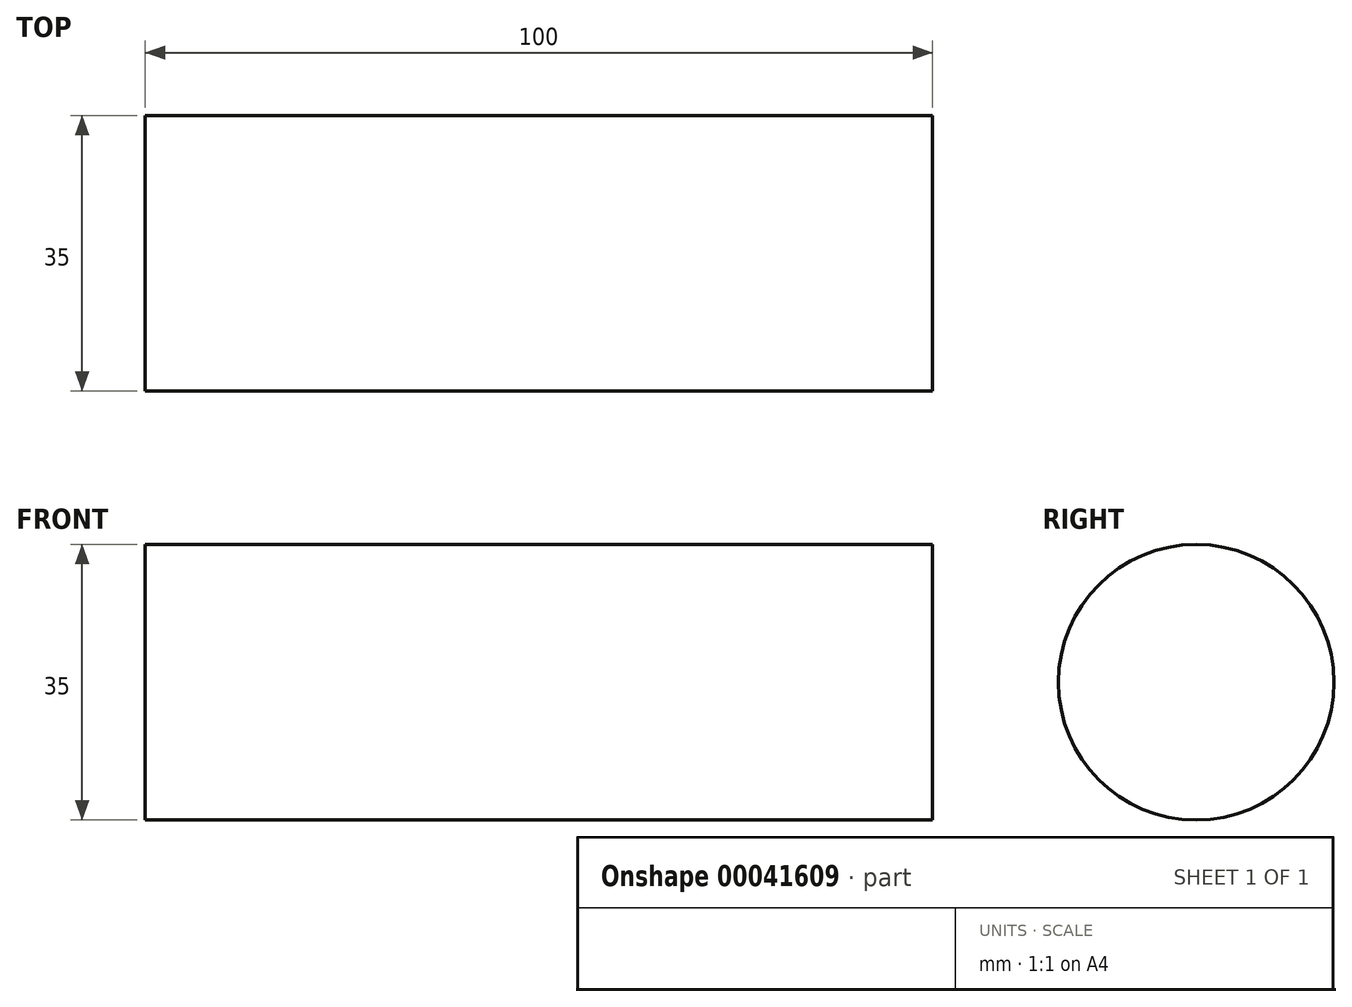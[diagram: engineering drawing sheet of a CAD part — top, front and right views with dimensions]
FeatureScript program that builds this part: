
annotation { "Feature Type Name" : "Feature", "Feature Type Description" : "" }
export const myFeature = defineFeature(function(context is Context, id is Id, definition is map)
    precondition{}
    {
        {
            var Q0;
            Q0=qCreatedBy(makeId("Front.planeOp"),FACE);
            var sketch = newSketch(context, id + "F0", { "sketchPlane" : qUnion([Q0])});
            skLineSegment(sketch, "E0.rect.bottom", {"start": v(100, 17.5) * mm, "end": v(0, 17.5) * mm});
            skLineSegment(sketch, "E0.rect.top", {"start": v(100, -17.5) * mm, "end": v(0, -17.5) * mm, "construction": true});
            skLineSegment(sketch, "E0.rect.left", {"start": v(100, 17.5) * mm, "end": v(100, -17.5) * mm, "construction": true});
            skLineSegment(sketch, "E0.rect.right", {"start": v(0, 17.5) * mm, "end": v(0, -17.5) * mm, "construction": true});
            skPoint(sketch, "E0.rect.middle", {"position": v(50, 0) * mm});
            skLineSegment(sketch, "E1", {"start": v(0, 0) * mm, "end": v(100, 0) * mm});
            skLineSegment(sketch, "E2", {"start": v(0, 17.5) * mm, "end": v(0, 0) * mm});
            skLineSegment(sketch, "E3", {"start": v(100, 17.5) * mm, "end": v(100, 0) * mm});
            skSolve(sketch);
        }
        {
            var Q0;
            Q0=makeQuery(id+"F0.imprint","IMPRINT",FACE,{"disambiguationData":[TD([[makeQuery(id+"F0.imprint","IMPRINT",EDGE,{"derivedFrom":sQuery(id+"F0.wireOp",EDGE,"E0.rect.bottom")}),1.0]])]});
            var Q1;
            Q1=sQuery(id+"F0.wireOp",EDGE,"E1");
            revolve(context, id + "F1", {"entities" : qUnion([Q0]), "axis" : qUnion([Q1]), "revolveType" : RevolveType.FULL});
        }
    });
